# Revit family: Gorter BVA 600x600mm
name_source: partatom
category: Generic Models
units: mm (PartAtom-declared; Revit-internal decimal feet)

## family parameters
Can host rebar = No
Cut with Voids When Loaded = Yes
Host = Face
Part Type = Normal
Room Calculation Point = No
Round Connector Dimension = Use Diameter
Shared = Yes

## types (5) — shared parameters
Manufacturer = Gorter
Model = BVA
belasting = 125 kN
binnenluik = tbv betonvulling
brandwerend 90 min = nee
gasdrukveer = nee
geïsoleerd = nee
materiaal = bcb_aluminium
rubberen_afdichting = enkel
scharnierend = nee
sluiting hoek = Yes
vergrendeling = nee
vullen_met_beton = ja
zero-valued in all types: Default Elevation

## per-type parameters (varying)
| type | Description | binnenmaat_breedte | binnenmaat_lengte | gewicht | sluiting | sluiting x-as | sluiting y-as | uitwendige_breedte | uitwendige_lengte |
| BVA 600x400mm | BVA 64 | 600 mm | 400 mm  [stored 1.31234 ft] | 9 | 4 | No | No | 720 mm  [stored 2.3622 ft] | 520 mm |
| BVA 600x600mm | BVA 66 | 600 mm | 600 mm | 9 | 4 | No | No | 720 mm  [stored 2.3622 ft] | 720 mm  [stored 2.3622 ft] |
| BVA 800x600mm | BVA 86 | 800 mm | 600 mm | 12 | 8 | No | Yes | 920 mm | 720 mm  [stored 2.3622 ft] |
| BVA 800x800mm | BVA 88 | 800 mm | 800 mm | 15 | 8 | Yes | Yes | 920 mm | 920 mm |
| BVA 1000x600mm | BVA 106 | 1000 mm  [stored 3.28084 ft] | 600 mm | 15 | 6 | No | Yes | 1120 mm | 720 mm  [stored 2.3622 ft] |

note: [stored X ft] marks values corroborated as IEEE doubles in the binary element streams (Revit-internal decimal feet)

## geometry (parser evidence)
native form markers: Blend x281, Sweep x8
no freeform markers — native parametric forms only
